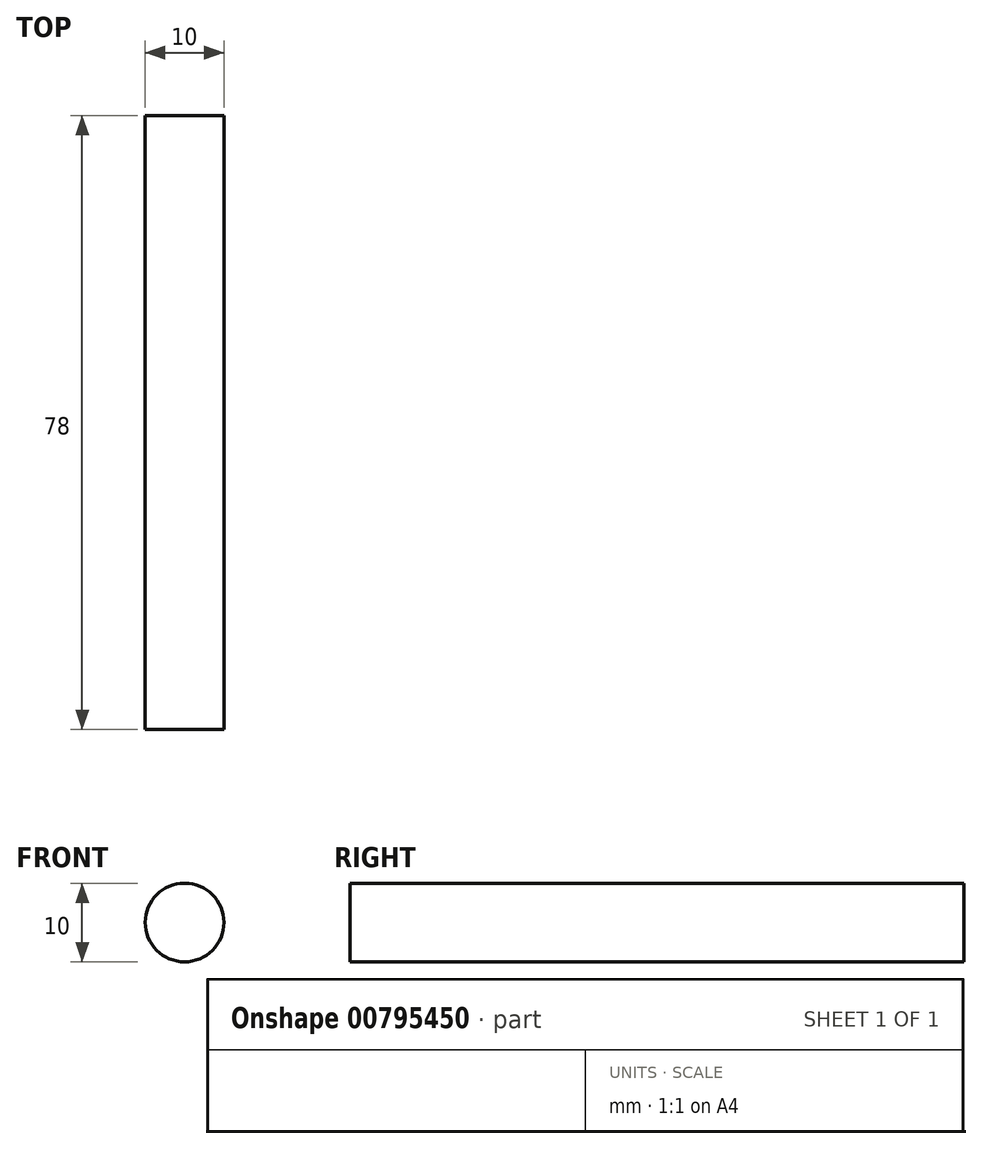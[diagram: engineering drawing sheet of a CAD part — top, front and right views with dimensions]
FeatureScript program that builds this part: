
annotation { "Feature Type Name" : "Feature", "Feature Type Description" : "" }
export const myFeature = defineFeature(function(context is Context, id is Id, definition is map)
    precondition{}
    {
        {
            var Q0;
            Q0=qCreatedBy(makeId("Front.planeOp"),FACE);
            var sketch = newSketch(context, id + "F0", { "sketchPlane" : qUnion([Q0])});
            skCircle(sketch, "E0", {"center": v(0, 0) * mm, "radius": 5 * mm});
            skSolve(sketch);
        }
        {
            var Q0;
            Q0=qSketchRegion(id+"F0",true);
            extrude(context, id + "F1", {"entities" : qUnion([Q0]), "depth" : 90 * mm, "offsetDistance" : 25 * mm});
        }
        {
            var Q0;
            Q0=makeQuery(id+"F1.opExtrude","CAP_FACE",FACE,{"disambiguationData":[OSD([sQuery(id+"F0.wireOp",EDGE,"E0")])],"isStart":false});
            extrude(context, id + "F2", {"entities" : qUnion([Q0]), "operationType" : NewBodyOperationType.REMOVE, "oppositeDirection" : true, "depth" : 12 * mm, "offsetDistance" : 25 * mm});
        }
    });
